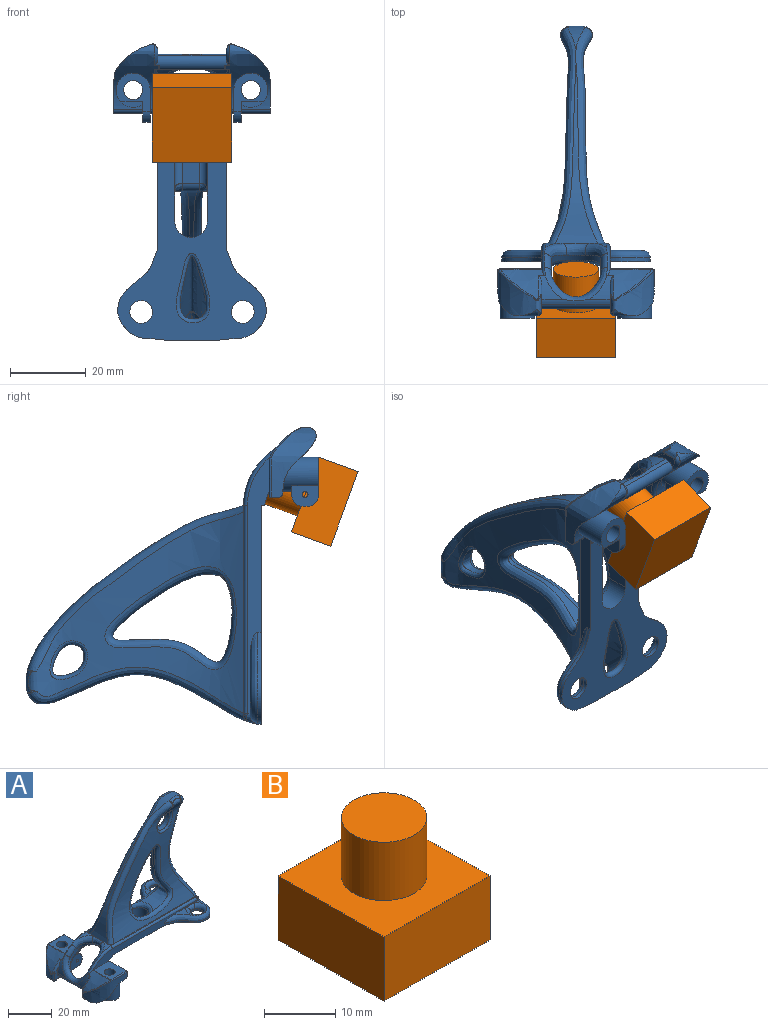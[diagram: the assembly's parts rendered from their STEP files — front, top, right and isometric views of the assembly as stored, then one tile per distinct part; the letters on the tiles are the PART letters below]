
ASSEMBLY  parts=2 mates=1
PART A: 179 faces, bbox 78.9x41.9x77.7 mm
  f0: plane 10.01x9mm, normal (0,0,-1), area 43.7mm2, adj f1,f3,f174,f176,f177,f178
  f1: plane 7x5.76mm, normal (1,0,0), area 40.3mm2, adj f0,f2,f3,f177
  f2: plane 5.76x1.4mm, normal (0,0,-1), area 6mm2, adj f1,f3,f177
  f3: cylinder r=4.5mm len=9.4mm, axis (0,0,1), area 142mm2, adj f0,f1,f2,f4,f7,f174
  f4: plane 5.47x2mm, normal (0,0,1), area 5.8mm2, adj f3,f5,f174,f177
  f5: cylinder r=3mm len=3mm, axis (0,1,0), area 9.4mm2, adj f4,f6,f174,f177
  f6: plane 2x1mm, normal (1,0,0), area 2mm2, adj f5,f174,f176,f177
  f7: extruded ~17.24x12.18mm, area 112.9mm2, adj f3,f8,f169,f170,f171,f172,f173
  f8: cylinder r=1mm len=10.66mm, axis (0,-1,0), area 16.9mm2, adj f7,f9,f168,f169
  f9: sphere r=1mm, area 1.6mm2, adj f8,f10,f173
  f10: cylinder r=1mm len=2.59mm, axis (0,0,1), area 4.1mm2, adj f9,f11,f167,f168
  f11: plane 7.45x4.96mm, normal (0,-1,0), area 9.8mm2, adj f10,f12,f167,f173
  f12: cylinder r=20.59mm len=13.73mm, axis (0,1,0), area 38.1mm2, adj f11,f13,f163,f164,f165,f166,f172,f173
  f13: torus R=22.59mm, axis (0,1,0), area 14.9mm2, adj f12,f14,f163,f166
  f14: plane 5.24x4.64mm, normal (0,-1,0), area 10.3mm2, adj f13,f15,f161,f162
  f15: torus R=16.46mm, axis (0,1,0), area 15.3mm2, adj f14,f16,f159,f160
  f16: bspline ~17x10.99mm, area 90.5mm2, adj f15,f17,f151,f152,f153,f154,f155,f156
  f17: cylinder r=3.64mm len=18mm, axis (0,1,0), area 21.3mm2, adj f16,f18,f141,f151,f158,f172
  f18: plane 6.86x2.94mm, normal (0,1,0), area 9.6mm2, adj f17,f19,f139,f140,f158,f172
  f19: bspline ~6.97x6.28mm, area 8.6mm2, adj f18,f20,f139,f157,f158
  f20: bspline ~1.31x1.2mm, area 0.5mm2, adj f19,f21,f138,f139
  f21: extruded ~18.24x11.92mm, area 142.4mm2, adj f20,f22,f134,f135,f137,f138,f139,f140
  f22: plane 10.67x2.61mm, normal (1,0,0), area 27.6mm2, adj f21,f23,f121,f134,f137
  f23: cylinder r=1mm len=2.59mm, axis (0,0,1), area 4.1mm2, adj f22,f24,f120,f121
  f24: plane 7.47x4.96mm, normal (0,1,0), area 9.8mm2, adj f23,f25,f119,f121
  f25: cylinder r=20.59mm len=13.73mm, axis (0,1,0), area 38.1mm2, adj f24,f26,f28,f112,f117,f119,f166,f172
  f26: torus R=22.59mm, axis (0,1,0), area 14.9mm2, adj f25,f27,f117,f166
  f27: plane 5.24x4.64mm, normal (0,1,0), area 10.3mm2, adj f26,f154,f155,f161
  f28: plane 6.48x1.03mm, normal (1,0,0), area 4.3mm2, adj f25,f29,f112,f166
  f29: plane 18.12x5.82mm, normal (0,0,-1), area 99.8mm2, adj f28,f30,f112,f164,f165,f166
  f30: cylinder r=1mm len=18mm, axis (0,1,0), area 4.9mm2, adj f29,f31,f112,f164
  f31: plane 51.74x39.44mm, normal (0,0,-1), area 867.2mm2, adj f30,f32,f101,f102,f103,f104,f105,f106
  f32: cylinder r=3mm len=6mm, axis (0,0,-1), area 18.8mm2, adj f31,f33,f100
  f33: torus R=5mm, axis (0,0,-1), area 57.5mm2, adj f32,f34,f35,f99,f100
  f34: plane 8.83x6.79mm, normal (0,0,1), area 19.8mm2, adj f33,f35,f164
  f35: bspline ~25.98x14.17mm, area 97.2mm2, adj f33,f34,f36,f37,f99,f111,f164
  f36: extruded ~1.9x0.22mm, area 0.1mm2, adj f35,f37,f111
  f37: bspline ~5.49x3.14mm, area 3.9mm2, adj f35,f36,f38,f98,f99,f109,f164
  f38: bspline ~2.23x1.97mm, area 1.5mm2, adj f37,f39,f98
  f39: cylinder r=2mm len=1.97mm, axis (0,1,0), area 2.2mm2, adj f38,f40,f96,f109
  f40: bspline ~58.93x14.68mm, area 189.5mm2, adj f39,f41,f91,f92,f93,f94,f95,f96
  f41: bspline ~58.96x14.68mm, area 189.3mm2, adj f40,f42,f69,f70,f86,f87,f91,f95
  f42: cylinder r=2mm len=1.91mm, axis (0,1,0), area 1.7mm2, adj f41,f43,f69,f109
  f43: bspline ~2.23x1.97mm, area 1.5mm2, adj f42,f44,f51
  f44: bspline ~5.49x3.14mm, area 3.9mm2, adj f43,f45,f46,f50,f51,f109,f112
  f45: extruded ~1.9x0.22mm, area 0.1mm2, adj f44,f46,f107
  f46: bspline ~25.97x14.17mm, area 97.2mm2, adj f44,f45,f47,f48,f50,f107,f112
  f47: plane 8.83x6.79mm, normal (0,0,1), area 19.8mm2, adj f46,f48,f112
  f48: torus R=5mm, axis (0,0,-1), area 57.5mm2, adj f46,f47,f49,f50,f106
  f49: bspline ~5.47x2.3mm, area 9.7mm2, adj f48,f106,f112
  f50: plane 3.68x2.8mm, normal (0,0,1), area 3.6mm2, adj f44,f46,f48,f112
  f51: bspline ~1.3x1.12mm, area 0.8mm2, adj f43,f44,f52,f69
  f52: cylinder r=1mm len=54.87mm, axis (-1,0,0), area 86.2mm2, adj f51,f53,f69,f112
  f53: sphere r=1mm, area 0mm2, adj f52,f54,f156
  f54: cylinder r=1mm len=0.46mm, axis (0,1,0), area 0mm2, adj f53,f55,f56,f69
  f55: extruded ~0.01x0mm, area 0mm2, adj f54,f69
  f56: cylinder r=18.46mm len=6.13mm, axis (0,1,0), area 10.7mm2, adj f54,f57,f68,f69,f156
  f57: extruded ~47.23x28.36mm, area 135.5mm2, adj f56,f58,f59,f60,f64
  f58: bspline ~7.49x3.46mm, area 21.5mm2, adj f57,f68,f160,f161
  f59: cylinder r=18.46mm len=6.13mm, axis (0,1,0), area 14.2mm2, adj f57,f96,f159,f160
  f60: bspline ~57.23x44.29mm, area 234mm2, adj f57,f61,f63,f64,f91,f93,f96
  f61: bspline ~1.85x1.22mm, area 0.2mm2, adj f60,f62,f63
  f62: bspline ~6.44x2.19mm, area 10.9mm2, adj f61,f91,f92,f93
  f63: bspline ~0.99x0.27mm, area 0.1mm2, adj f60,f61,f93
  f64: bspline ~57.16x44.13mm, area 234.6mm2, adj f57,f60,f65,f67,f69,f70,f91
  f65: bspline ~1.73x0.99mm, area 0.3mm2, adj f64,f66,f67
  f66: bspline ~6.29x2.13mm, area 9.6mm2, adj f65,f70,f86,f91
  f67: bspline ~1.71x0.39mm, area 0.2mm2, adj f64,f65,f70
  f68: bspline ~11.19x7.44mm, area 34mm2, adj f56,f58,f155,f156,f161
  f69: plane 55.79x2.85mm, normal (0,0,1), area 25.9mm2, adj f41,f42,f51,f52,f54,f55,f56,f64
  f70: extruded ~56.82x52.89mm, area 999.9mm2, adj f41,f64,f66,f67,f69,f71,f83,f86
  f71: bspline ~34.63x27.05mm, area 270.2mm2, adj f70,f72,f80,f81,f82
  f72: bspline ~12.61x7.23mm, area 44.2mm2, adj f71,f73,f79,f80,f82,f104
  f73: bspline ~10.48x4.64mm, area 13.3mm2, adj f72,f74,f79,f103
  f74: bspline ~4.86x4.72mm, area 10.9mm2, adj f73,f75,f78,f79
  f75: cylinder r=2mm len=11.85mm, axis (1,0,0), area 29.8mm2, adj f74,f76,f102,f103
  f76: plane 9.68x4.61mm, normal (0,0,-1), area 43.8mm2, adj f75,f77,f78,f102
  f77: cylinder r=2mm len=11.85mm, axis (-1,0,0), area 29.8mm2, adj f76,f81,f101,f102
  f78: cylinder r=2mm len=4.61mm, axis (0,1,0), area 16.6mm2, adj f74,f76,f79,f80,f81
  f79: bspline ~34.67x27.19mm, area 258.2mm2, adj f72,f73,f74,f78,f80,f93
  f80: extruded ~31.35x23.12mm, area 203.1mm2, adj f71,f72,f78,f79,f81
  f81: bspline ~4.86x4.72mm, area 11.8mm2, adj f71,f77,f78,f80,f82
  f82: bspline ~10.48x4.64mm, area 17.1mm2, adj f71,f72,f81,f101
  f83: bspline ~10.23x9.89mm, area 42mm2, adj f70,f84
  f84: extruded ~8.28x8.21mm, area 60.8mm2, adj f83,f85
  f85: bspline ~10.22x9.91mm, area 42.1mm2, adj f84,f93
  f86: bspline ~2.58x2.02mm, area 0.6mm2, adj f41,f66,f70
  f87: bspline ~7.42x4.66mm, area 13.4mm2, adj f41,f88,f89,f90
  f88: bspline ~4.67x3.43mm, area 7.8mm2, adj f87,f89,f94,f95
  f89: extruded ~21.96x21.96mm, area 337mm2, adj f87,f88,f90,f94,f105
  f90: bspline ~8.86x3.84mm, area 20.6mm2, adj f87,f89,f94,f109
  f91: extruded ~20.18x8.9mm, area 73.9mm2, adj f40,f41,f60,f62,f64,f66
  f92: bspline ~2.1x2mm, area 0.5mm2, adj f40,f62,f93
  f93: extruded ~56.76x52.96mm, area 1002mm2, adj f40,f60,f62,f63,f79,f85,f92,f96
  f94: bspline ~7.35x4.62mm, area 13.3mm2, adj f40,f88,f89,f90
  f95: extruded ~36x7.04mm, area 87.7mm2, adj f40,f41,f88
  f96: plane 55.82x3.12mm, normal (0,0,1), area 39.8mm2, adj f39,f40,f59,f60,f93,f97,f98
  f97: cylinder r=1mm len=54.88mm, axis (1,0,0), area 86.2mm2, adj f96,f98,f159,f164
  f98: bspline ~1.3x1.12mm, area 0.8mm2, adj f37,f38,f96,f97
  f99: plane 3.68x2.8mm, normal (0,0,1), area 3.6mm2, adj f33,f35,f37,f164
  f100: bspline ~5.47x2.3mm, area 9.7mm2, adj f32,f33,f164
  f101: plane 17.1x8mm, normal (0,1,0), area 126.7mm2, adj f31,f77,f82,f102,f104
  f102: cylinder r=4.88mm len=10mm, axis (0,0,-1), area 99.8mm2, adj f31,f75,f76,f77,f101,f103
  f103: plane 17.11x8.01mm, normal (0,-1,0), area 126.7mm2, adj f31,f73,f75,f102,f104
  f104: cylinder r=4.31mm len=8.61mm, axis (0,0,-1), area 79.5mm2, adj f31,f72,f101,f103
  f105: bspline ~18.31x8.87mm, area 62.3mm2, adj f31,f89
  f106: cylinder r=3mm len=6mm, axis (0,0,-1), area 18.8mm2, adj f31,f48,f49
  f107: extruded ~24.16x12.58mm, area 36.6mm2, adj f31,f45,f46,f108,f112
  f108: bspline ~2.11x2mm, area 0.2mm2, adj f31,f107
  f109: extruded ~14x7.95mm, area 68.2mm2, adj f31,f37,f39,f40,f41,f42,f44,f90
  f110: bspline ~2.11x2mm, area 0.2mm2, adj f31,f111
  f111: extruded ~24.16x12.58mm, area 36.6mm2, adj f31,f35,f36,f110,f164
  f112: plane 67.73x5.87mm, normal (0,-1,0), area 190.2mm2, adj f25,f28,f29,f30,f31,f44,f46,f47
  f113: cylinder r=0.5mm len=5.6mm, axis (0,1,0), area 1.3mm2, adj f112,f114,f121,f156,f157
  f114: cylinder r=4.5mm len=3.35mm, axis (0,0,1), area 0.1mm2, adj f113,f115,f121,f157
  f115: cylinder r=0.5mm len=3.52mm, axis (0,1,0), area 0.8mm2, adj f114,f116,f121,f157
  f116: sphere r=0.5mm, area 0.1mm2, adj f115,f134,f138
  f117: bspline ~8.35x6.27mm, area 23.1mm2, adj f25,f26,f118,f154
  f118: bspline ~7.75x2.23mm, area 10.8mm2, adj f117,f153,f154,f162,f163,f172
  f119: bspline ~13.47x8.11mm, area 17.7mm2, adj f24,f25,f120,f135,f172
  f120: sphere r=1mm, area 1.6mm2, adj f23,f119,f137
  f121: plane 11.18x10.56mm, normal (0,0,1), area 94.8mm2, adj f22,f23,f24,f112,f113,f114,f115,f122
  f122: cylinder r=2.5mm len=13mm, axis (0,0,-1), area 204.2mm2, adj f121,f123
  f123: plane 10.01x9mm, normal (0,0,-1), area 43.7mm2, adj f122,f124,f129,f130,f132,f133
  f124: cylinder r=4.5mm len=9.4mm, axis (0,0,1), area 142.1mm2, adj f123,f125,f128,f129,f133,f135
  f125: plane 5.47x2mm, normal (0,0,1), area 5.8mm2, adj f124,f126,f130,f133
  f126: cylinder r=3mm len=3mm, axis (0,1,0), area 9.4mm2, adj f125,f127,f130,f133
  f127: plane 2x1mm, normal (1,0,0), area 2mm2, adj f126,f130,f132,f133
  f128: plane 5.76x1.4mm, normal (0,0,-1), area 6mm2, adj f124,f129,f130
  f129: plane 7x5.76mm, normal (1,0,0), area 40.3mm2, adj f123,f124,f128,f130
  f130: plane 7x5.41mm, normal (0,-1,0), area 32.2mm2, adj f123,f125,f126,f127,f128,f129,f131,f132
  f131: cylinder r=0.75mm len=2mm, axis (0,-1,0), area 9.4mm2, adj f130,f133
  f132: cylinder r=3mm len=3mm, axis (0,1,0), area 9.4mm2, adj f123,f127,f130,f133
  f133: plane 8.47x7mm, normal (0,1,0), area 53.6mm2, adj f123,f124,f125,f126,f127,f131,f132
  f134: bspline ~13.33x0.88mm, area 8.1mm2, adj f21,f22,f116,f121
  f135: extruded ~17.24x12.18mm, area 113mm2, adj f21,f119,f124,f136,f137,f140,f172
  f136: torus R=1.5mm, axis (0,-1,0), area 29.6mm2, adj f135,f172
  f137: cylinder r=1mm len=10.66mm, axis (0,1,0), area 16.9mm2, adj f21,f22,f120,f135
  f138: bspline ~10.99x8.39mm, area 7.5mm2, adj f20,f21,f116,f157
  f139: plane 4.98x0.34mm, normal (-1,0,0), area 0.7mm2, adj f18,f19,f20,f21,f140
  f140: bspline ~6.45x3.42mm, area 7.7mm2, adj f18,f21,f135,f139,f172
  f141: plane 6.86x2.94mm, normal (0,-1,0), area 9.6mm2, adj f17,f142,f150,f151,f170,f172
  f142: bspline ~7.33x6.45mm, area 8.6mm2, adj f141,f143,f150,f151,f152
  f143: bspline ~1.31x1.2mm, area 0.5mm2, adj f142,f144,f150,f169
  f144: bspline ~10.99x8.39mm, area 7.5mm2, adj f143,f145,f152,f169
  f145: sphere r=0.5mm, area 0.1mm2, adj f144,f146,f149
  f146: cylinder r=0.5mm len=3.52mm, axis (0,-1,0), area 0.8mm2, adj f145,f147,f152,f167
  f147: cylinder r=4.5mm len=3.35mm, axis (0,0,1), area 0.1mm2, adj f146,f148,f152,f167
  f148: cylinder r=0.5mm len=5.6mm, axis (0,-1,0), area 1.3mm2, adj f147,f152,f159,f164,f167
  f149: bspline ~13.33x0.88mm, area 8.1mm2, adj f145,f167,f168,f169
  f150: plane 4.99x0.34mm, normal (-1,0,0), area 0.7mm2, adj f141,f142,f143,f169,f170
  f151: cylinder r=18.46mm len=6.52mm, axis (0,1,0), area 23.1mm2, adj f16,f17,f141,f142,f152
  f152: extruded ~11.87x8.16mm, area 72.5mm2, adj f16,f142,f144,f146,f147,f148,f151,f159
  f153: cylinder r=6.5mm len=4.4mm, axis (-0.64,0,0.77), area 1.3mm2, adj f16,f118
  f154: cylinder r=6.5mm len=6.99mm, axis (-0.64,0,0.77), area 9mm2, adj f16,f27,f117,f118
  f155: torus R=16.46mm, axis (0,1,0), area 15.3mm2, adj f16,f27,f68,f156
  f156: torus R=17.46mm, axis (0,-1,0), area 24.1mm2, adj f16,f53,f56,f68,f112,f113,f155,f157
  f157: extruded ~11.87x8.16mm, area 72.5mm2, adj f16,f19,f113,f114,f115,f138,f156,f158
  f158: cylinder r=18.46mm len=6.52mm, axis (0,1,0), area 23.1mm2, adj f16,f17,f18,f19,f157
  f159: torus R=17.46mm, axis (0,-1,0), area 24.1mm2, adj f15,f16,f59,f97,f148,f152,f160,f164
  f160: bspline ~11.06x7.32mm, area 34mm2, adj f15,f58,f59,f159,f161
  f161: cylinder r=6.5mm len=13mm, axis (-0.64,0,0.77), area 39.4mm2, adj f14,f27,f58,f68,f160,f166
  f162: cylinder r=6.5mm len=6.99mm, axis (-0.64,0,0.77), area 9mm2, adj f14,f16,f118,f163
  f163: bspline ~8.33x6.23mm, area 23.1mm2, adj f12,f13,f118,f162
  f164: plane 67.73x5.87mm, normal (0,1,0), area 190.2mm2, adj f12,f29,f30,f31,f34,f35,f37,f97
  f165: plane 6.46x1mm, normal (1,0,0), area 4.3mm2, adj f12,f29,f164,f166
  f166: bspline ~17x8.92mm, area 43.1mm2, adj f12,f13,f25,f26,f28,f29,f161,f165
  f167: plane 11.18x10.56mm, normal (0,0,1), area 94.8mm2, adj f10,f11,f146,f147,f148,f149,f164,f168
  f168: plane 10.67x2.61mm, normal (1,0,0), area 27.6mm2, adj f8,f10,f149,f167,f169
  f169: extruded ~18.24x11.92mm, area 142.4mm2, adj f7,f8,f143,f144,f149,f150,f168,f170
  f170: bspline ~6.45x3.42mm, area 7.7mm2, adj f7,f141,f150,f169,f172
  f171: torus R=1.5mm, axis (0,-1,0), area 29.6mm2, adj f7,f172
  f172: cylinder r=2mm len=20mm, axis (0,-1,0), area 82.5mm2, adj f7,f12,f17,f18,f25,f118,f119,f135
  f173: bspline ~13.47x8.11mm, area 17.7mm2, adj f7,f9,f11,f12,f172
  f174: plane 8.47x7mm, normal (0,-1,0), area 53.6mm2, adj f0,f3,f4,f5,f6,f175,f176
  f175: cylinder r=0.75mm len=2mm, axis (0,1,0), area 9.4mm2, adj f174,f177
  f176: cylinder r=3mm len=3mm, axis (0,1,0), area 9.4mm2, adj f0,f6,f174,f177
  f177: plane 7x5.41mm, normal (0,1,0), area 32.2mm2, adj f0,f1,f2,f4,f5,f6,f175,f176
  f178: cylinder r=2.5mm len=13mm, axis (0,0,-1), area 204.2mm2, adj f0,f167
PART B: 8 faces, bbox 21x21x21 mm
  f0: plane 21x11mm, normal (0,1,0), area 231mm2, adj f1,f3,f4,f5
  f1: plane 21x11mm, normal (-1,0,0), area 231mm2, adj f0,f2,f4,f5
  f2: plane 21x11mm, normal (0,-1,0), area 231mm2, adj f1,f3,f4,f5
  f3: plane 21x11mm, normal (1,0,0), area 231mm2, adj f0,f2,f4,f5
  f4: plane 21x21mm, normal (0,0,1), area 327.9mm2, adj f0,f1,f2,f3,f6
  f5: plane 21x21mm, normal (0,0,-1), area 441mm2, adj f0,f1,f2,f3
  f6: cylinder r=6mm len=12mm, axis (0,0,-1), area 377mm2, adj f4,f7
  f7: plane 12x12mm, normal (0,0,1), area 113.1mm2, adj f6
PLACE A rot(axis=(-0.58,0.58,0.58),120deg) t=(-20.71,11.68,46.7)mm
PLACE B rot(axis=(-0.5,0.5,0.71),109.2deg) t=(-22.21,5.25,56.56)mm
MATE revolute B.f2 <-> A.f131  axis (1,0,0) through (-1.21,19.18,50.46)mm
